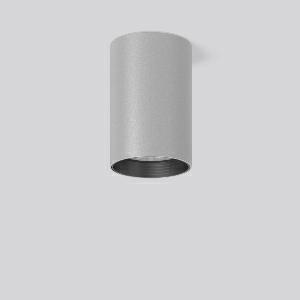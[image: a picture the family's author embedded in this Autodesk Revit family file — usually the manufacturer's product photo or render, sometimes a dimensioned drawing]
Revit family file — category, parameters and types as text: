
# Revit family: heledon_maxi_a_931227_004_76_7dfe
name_source: partatom
category: Lighting Fixtures
units: mm (PartAtom-declared; Revit-internal decimal feet)

## family parameters
Cut with Voids When Loaded = No
Host = Face
Light Source = No
Part Type = Normal
Room Calculation Point = No
Round Connector Dimension = Use Diameter
Shared = No

## types (1)
- HELEDON maxi A (1 x LED Modul 930, 3650 lm, 3000)
    Apparent Load = 35 VA
    Approval mark = CE
    CIE Flux Codes = 97 100 100 100 100
    Color Rendering = 90
    Color Temperature = 3000
    Default Elevation = 1800 mm
    Description = Series: HELEDON maxi
Cylindrical surface-mounted downlight. Housing: die-cast aluminium, powder-coated. Internal ceiling frame polycarbonate with bayonet mounting. Black plastic ring and recessed LED to prevent glare from the side. Optical assembly with lens made of plastic (polycarbonate) for the best homogeneous light distribution - can be changed without tools. Best colour rendering index Ra>90. Suitable for Ceiling mounting. Easy installation with a separate ceiling frame with bayonet mounting and plug connection. Driver integrated. Connected via plug-in connector. High quality converter without flickering and stroboscopic effect. The following accessories can be mounted without use of tools: interchangeable lenses, decorative glasses, honeycomb louvre, clear and frosted diffusers, white interchangeable plastic ring. 
Colour: silver
Diameter: 123 mm
Height: 183 mm
Lamp: LED
Socket: without socket
Colour temperature: 3000K
Colour rendering index (CRI): 92
System power: 35 W
Rated luminous flux: 3650 lm
Luminous efficiency: 104 lm/W
Control gear: Converter, dimmable, DALI
Protection class: I
Type of protection: IP 20
    Height = 183 mm
    Lamp = 1 x LED Modul 930
    Lamp Light Flux = 3650 lm
    Lamp count = 1
    Length = 123 mm
    Lifetime = 50000 h
    Luminous efficacy = 104 lm/W
    Manufacturer = RZB
    ModVariant = No
    Model = 931227.004.76
    Mounting Place = Ceiling
    Mounting Type = Surface mounted
    Number of Poles = 1
    OnlyDefault = Yes
    Power Factor = 1
    Product Name = HELEDON maxi A
    Product group = Surface mounted downlights
    ProductGroupID = 302
    Protection Class = Protection class I
    Protection Degree = IP 20
    RLX_Detail_Level = 1
    RLX_Emergency_Light_Flux = 0 lm
    RLX_Emergency_Type = 0
    RLX_Emergency_Type_DB = No
    RlxData = <blob elided: 100073 chars, md5=2eb9a481>
    Socket = socket
    Standby Power = 0 W
    System Light Flux = 3650 lm
    System Power = 35 W
    Type Comments = Product without accessories
    Type Image = 931193.004.jpg
    URL = http://relux.com
    VarID = ---
    Voltage = 230 V
    Voltage Range = 220-240 V
    Weight = 0.00 kg
    Width = 0 mm  [stored 0 ft]

note: [stored X ft] marks values corroborated as IEEE doubles in the binary element streams (Revit-internal decimal feet)

## geometry (parser evidence)
native form markers: Blend x4, Sweep x10
no freeform markers — native parametric forms only
